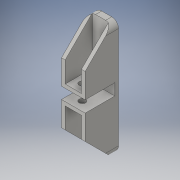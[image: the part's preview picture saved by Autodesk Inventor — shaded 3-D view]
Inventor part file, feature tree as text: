
AUTODESK INVENTOR PART (.ipt)
format: ipt  version: 2016 (Build 200138000, 138)  size: 182,272 bytes
history: native  units: in
note: dims shown in document units (in); Inventor stores cm internally (conversion verified against a paired STEP export)
features: extrude x8, sketch x8, chamfer x2, fillet x1
ambient origin geometry x8: Origin, YZ Plane, XZ Plane, XY Plane, X Axis, Y Axis, Z Axis, Center Point
bodies: Solid1 (feature_tree)
feature tree (19):
  extrude  "Extrusion1"  Depth=2.111in
  extrude  "Extrusion2"  Depth=0.95in
  extrude  "Extrusion3"  Depth=0.545in
  chamfer  "Chamfer1"  Distance=1.0in
  extrude  "Extrusion4"  Depth=0.068in
  extrude  "Extrusion5"  Depth=0.882in TaperAngle=0.0deg
  extrude  "Extrusion6"  Depth=0.545in TaperAngle=0.0deg
  chamfer  "Chamfer2"  Distance=1.545in
  extrude  "Extrusion7"  Depth=0.882in TaperAngle=0.0deg
  extrude  "Extrusion8"  Depth=0.125in
  fillet  "Fillet1"  Radius=0.1184in
  sketch  "Sketch1"  dims[d0=0.434in d1=2.111in]
  sketch  "Sketch2"  dims[d2=0.067in d3=0.0in d4=0.95in]
  sketch  "Sketch3"  dims[d5=0.545in d6=0.0in d7=0.1181in]
  sketch  "Sketch4"  dims[d8=0.1657in d9=1.0in d10=0.0in]
  sketch  "Sketch5"  dims[d11=0.5in d12=0.125in d13=45.0deg d14=0.068in]
  sketch  "Sketch6"  dims[d15=0.068in d16=0.882in d17=0.0in]
  sketch  "Sketch7"  dims[d18=0.95in d19=0.545in d20=0.0in d21=1.545in d22=0.0in]
  sketch  "Sketch8"  dims[d23=0.5in d24=0.125in d25=45.0deg d26=0.882in d27=0.0in d28=0.1181in d29=0.1184in d30=0.441in d31=0.441in d32=0.882in d33=0.0in d34=0.125in]
